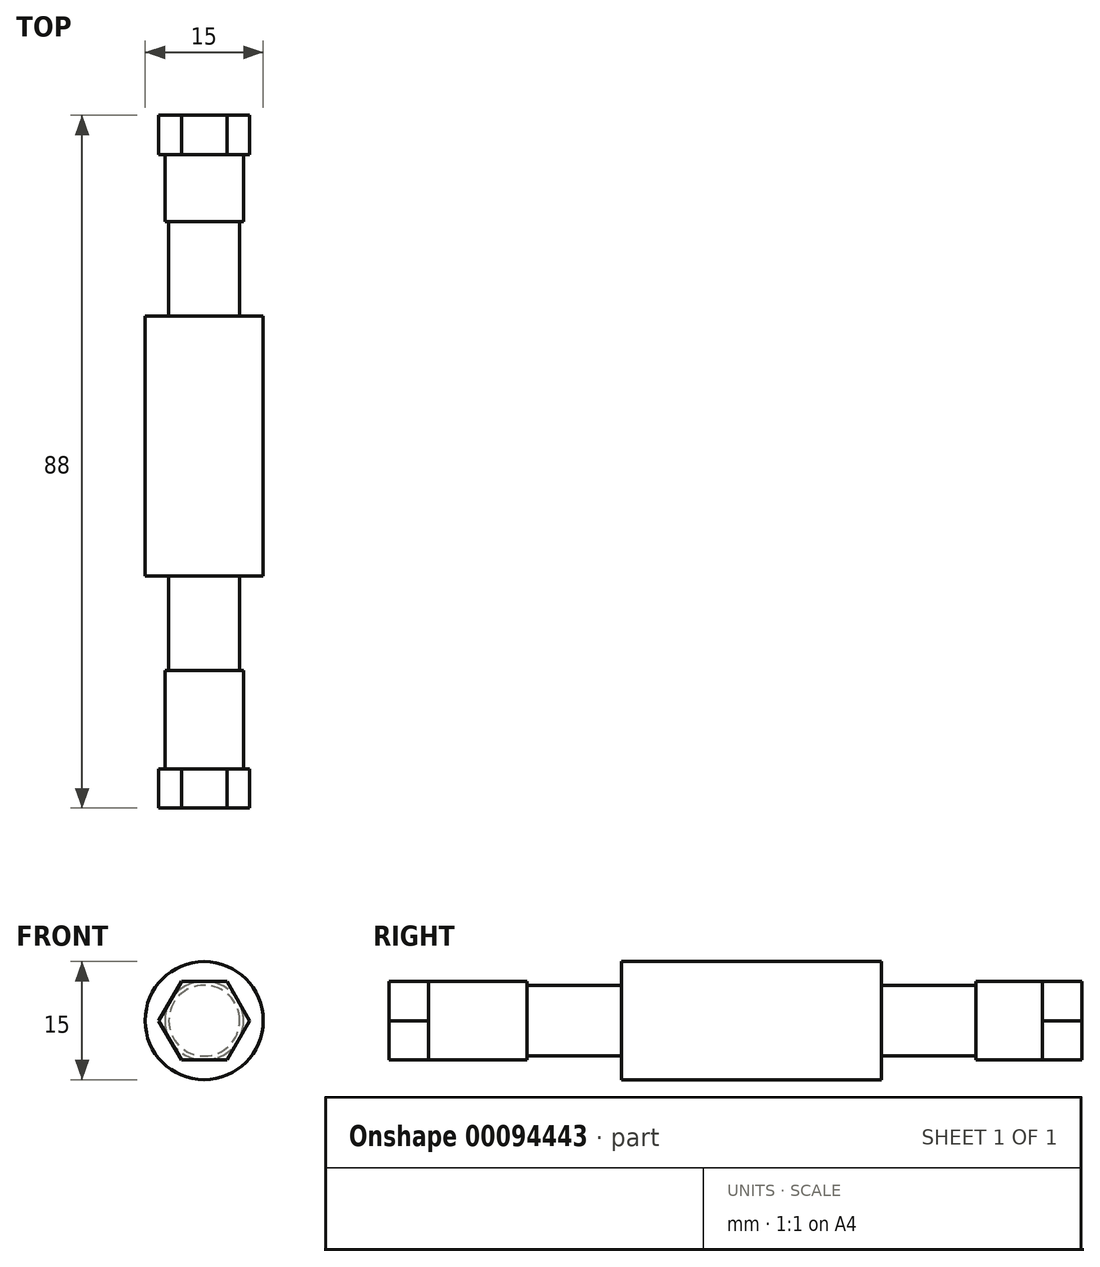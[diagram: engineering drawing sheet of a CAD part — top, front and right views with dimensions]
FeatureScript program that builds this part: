
annotation { "Feature Type Name" : "Feature", "Feature Type Description" : "" }
export const myFeature = defineFeature(function(context is Context, id is Id, definition is map)
    precondition{}
    {
        {
            var Q0;
            Q0=qCreatedBy(makeId("Front.planeOp"),FACE);
            var sketch = newSketch(context, id + "F0", { "sketchPlane" : qUnion([Q0])});
            skCircle(sketch, "E0", {"center": v(0, 0) * mm, "radius": 5 * mm});
            skSolve(sketch);
        }
        {
            var Q0;
            Q0=makeQuery(id+"F0.imprint","IMPRINT",FACE,{"disambiguationData":[TD([[makeQuery(id+"F0.imprint","IMPRINT",EDGE,{"derivedFrom":sQuery(id+"F0.wireOp",EDGE,"E0")}),1.0]])]});
            extrude(context, id + "F1", {"entities" : qUnion([Q0]), "depth" : 82 * mm});
        }
        {
            var Q0;
            Q0=makeQuery(id+"F1.opExtrude","CAP_FACE",FACE,{"disambiguationData":[OSD([sQuery(id+"F0.wireOp",EDGE,"E0")])],"isStart":false});
            var sketch = newSketch(context, id + "F2", { "sketchPlane" : qUnion([Q0])});
            skCircle(sketch, "E1.cCircle", {"center": v(0, 0) * mm, "radius": 5 * mm, "construction": true});
            skLineSegment(sketch, "E1.0", {"start": v(-2.89, 5) * mm, "end": v(2.89, 5) * mm});
            skLineSegment(sketch, "E1.1", {"start": v(2.89, 5) * mm, "end": v(5.77, 0) * mm});
            skLineSegment(sketch, "E1.2", {"start": v(5.77, 0) * mm, "end": v(2.89, -5) * mm});
            skLineSegment(sketch, "E1.3", {"start": v(2.89, -5) * mm, "end": v(-2.89, -5) * mm});
            skLineSegment(sketch, "E1.4", {"start": v(-2.89, -5) * mm, "end": v(-5.77, 0) * mm});
            skLineSegment(sketch, "E1.5", {"start": v(-5.77, 0) * mm, "end": v(-2.89, 5) * mm});
            skPoint(sketch, "E1.0.midPoint", {"position": v(0, 5) * mm});
            skSolve(sketch);
        }
        {
            var Q0;
            Q0=makeQuery(id+"F1.opExtrude","CAP_FACE",FACE,{"disambiguationData":[OSD([sQuery(id+"F0.wireOp",EDGE,"E0")])],"isStart":true});
            var sketch = newSketch(context, id + "F3", { "sketchPlane" : qUnion([Q0])});
            skCircle(sketch, "E2.cCircle", {"center": v(0, 0) * mm, "radius": 5 * mm, "construction": true});
            skLineSegment(sketch, "E2.0", {"start": v(-2.89, 5) * mm, "end": v(2.89, 5) * mm});
            skLineSegment(sketch, "E2.1", {"start": v(2.89, 5) * mm, "end": v(5.77, 0) * mm});
            skLineSegment(sketch, "E2.2", {"start": v(5.77, 0) * mm, "end": v(2.89, -5) * mm});
            skLineSegment(sketch, "E2.3", {"start": v(2.89, -5) * mm, "end": v(-2.89, -5) * mm});
            skLineSegment(sketch, "E2.4", {"start": v(-2.89, -5) * mm, "end": v(-5.77, 0) * mm});
            skLineSegment(sketch, "E2.5", {"start": v(-5.77, 0) * mm, "end": v(-2.89, 5) * mm});
            skPoint(sketch, "E2.0.midPoint", {"position": v(0, 5) * mm});
            skSolve(sketch);
        }
        {
            var Q0;
            Q0 = qSketchRegion(id + "F3", true);
            extrude(context, id + "F4", {"entities" : qUnion([Q0]), "operationType" : NewBodyOperationType.ADD, "oppositeDirection" : true, "depth" : 4 * mm});
        }
        {
            var Q0;
            Q0=qCreatedBy(makeId("Front.planeOp"),FACE);
            cPlane(context, id + "F5", {"entities" : qUnion([Q0]), "cplaneType" : CPlaneType.OFFSET, "offset" : 13.5 * mm, "width" : 150 * mm, "height" : 150 * mm});
        }
        {
            var Q0;
            Q0=qCreatedBy(id+"F5.planeOp",FACE);
            var sketch = newSketch(context, id + "F6", { "sketchPlane" : qUnion([Q0])});
            skCircle(sketch, "E3", {"center": v(0, 0) * mm, "radius": 4.5 * mm});
            skCircle(sketch, "E4", {"center": v(0, 0) * mm, "radius": 5.5 * mm});
            skSolve(sketch);
        }
        {
            var Q0;
            Q0 = qSketchRegion(id + "F6", true);
            extrude(context, id + "F7", {"entities" : qUnion([Q0]), "operationType" : NewBodyOperationType.REMOVE, "depth" : 11 * mm, "hasSecondDirection" : true, "secondDirectionOppositeDirection" : true, "secondDirectionDepth" : 1 * mm});
        }
        {
            var Q0;
            Q0=qCreatedBy(id+"F5.planeOp",FACE);
            cPlane(context, id + "F8", {"entities" : qUnion([Q0]), "cplaneType" : CPlaneType.OFFSET, "offset" : 45 * mm, "width" : 150 * mm, "height" : 150 * mm});
        }
        {
            var Q0;
            Q0=qCreatedBy(id+"F8.planeOp",FACE);
            var sketch = newSketch(context, id + "F9", { "sketchPlane" : qUnion([Q0])});
            skCircle(sketch, "E5", {"center": v(0, 0) * mm, "radius": 4.5 * mm});
            skCircle(sketch, "E6", {"center": v(0, 0) * mm, "radius": 5.5 * mm});
            skSolve(sketch);
        }
        {
            var Q0;
            Q0 = qSketchRegion(id + "F9", true);
            extrude(context, id + "F10", {"entities" : qUnion([Q0]), "operationType" : NewBodyOperationType.REMOVE, "depth" : 11 * mm, "hasSecondDirection" : true, "secondDirectionOppositeDirection" : true, "secondDirectionDepth" : 1 * mm});
        }
        {
            var Q0;
            Q0 = qSketchRegion(id + "F2", true);
            extrude(context, id + "F11", {"entities" : qUnion([Q0]), "operationType" : NewBodyOperationType.ADD, "depth" : 5 * mm});
        }
        {
            var Q0;
            Q0=qCreatedBy(id+"F8.planeOp",FACE);
            cPlane(context, id + "F12", {"entities" : qUnion([Q0]), "cplaneType" : CPlaneType.OFFSET, "offset" : (35 / 2) * mm, "oppositeDirection" : true, "width" : 150 * mm, "height" : 150 * mm});
        }
        {
            var Q0;
            Q0=qCreatedBy(id+"F12.planeOp",FACE);
            var sketch = newSketch(context, id + "F13", { "sketchPlane" : qUnion([Q0])});
            skCircle(sketch, "E7", {"center": v(0, 0) * mm, "radius": 7.5 * mm});
            skSolve(sketch);
        }
        {
            var Q0;
            Q0 = qSketchRegion(id + "F13", true);
            extrude(context, id + "F14", {"entities" : qUnion([Q0]), "operationType" : NewBodyOperationType.ADD, "depth" : 16.5 * mm, "hasSecondDirection" : true, "secondDirectionOppositeDirection" : true, "secondDirectionDepth" : 16.5 * mm});
        }
        {
            var Q0;
            Q0=makeQuery(id+"F4.boolean.opBoolean","MERGE",FACE,{"derivedFrom":[makeQuery(id+"F1.opExtrude","CAP_FACE",FACE,{"disambiguationData":[OSD([sQuery(id+"F0.wireOp",EDGE,"E0")])],"isStart":true}),makeQuery(id+"F4.opExtrude","CAP_FACE",FACE,{"disambiguationData":[OSD([sQuery(id+"F3.wireOp",EDGE,"E2.0"),sQuery(id+"F3.wireOp",EDGE,"E2.1"),sQuery(id+"F3.wireOp",EDGE,"E2.2"),sQuery(id+"F3.wireOp",EDGE,"E2.3"),sQuery(id+"F3.wireOp",EDGE,"E2.4"),sQuery(id+"F3.wireOp",EDGE,"E2.5")])],"isStart":true})]});
            var sketch = newSketch(context, id + "F15", { "sketchPlane" : qUnion([Q0])});
            skCircle(sketch, "E8.cCircle", {"center": v(0, 0) * mm, "radius": 5 * mm, "construction": true});
            skLineSegment(sketch, "E8.0", {"start": v(2.89, 5) * mm, "end": v(5.77, 0) * mm});
            skLineSegment(sketch, "E8.1", {"start": v(5.77, 0) * mm, "end": v(2.89, -5) * mm});
            skLineSegment(sketch, "E8.2", {"start": v(2.89, -5) * mm, "end": v(-2.89, -5) * mm});
            skLineSegment(sketch, "E8.3", {"start": v(-2.89, -5) * mm, "end": v(-5.77, 0) * mm});
            skLineSegment(sketch, "E8.4", {"start": v(-5.77, 0) * mm, "end": v(-2.89, 5) * mm});
            skLineSegment(sketch, "E8.5", {"start": v(-2.89, 5) * mm, "end": v(2.89, 5) * mm});
            skPoint(sketch, "E8.0.midPoint", {"position": v(4.33, 2.5) * mm});
            skSolve(sketch);
        }
        {
            var Q0;
            Q0 = qSketchRegion(id + "F15", true);
            extrude(context, id + "F16", {"entities" : qUnion([Q0]), "operationType" : NewBodyOperationType.ADD, "depth" : 1 * mm});
        }
    });
